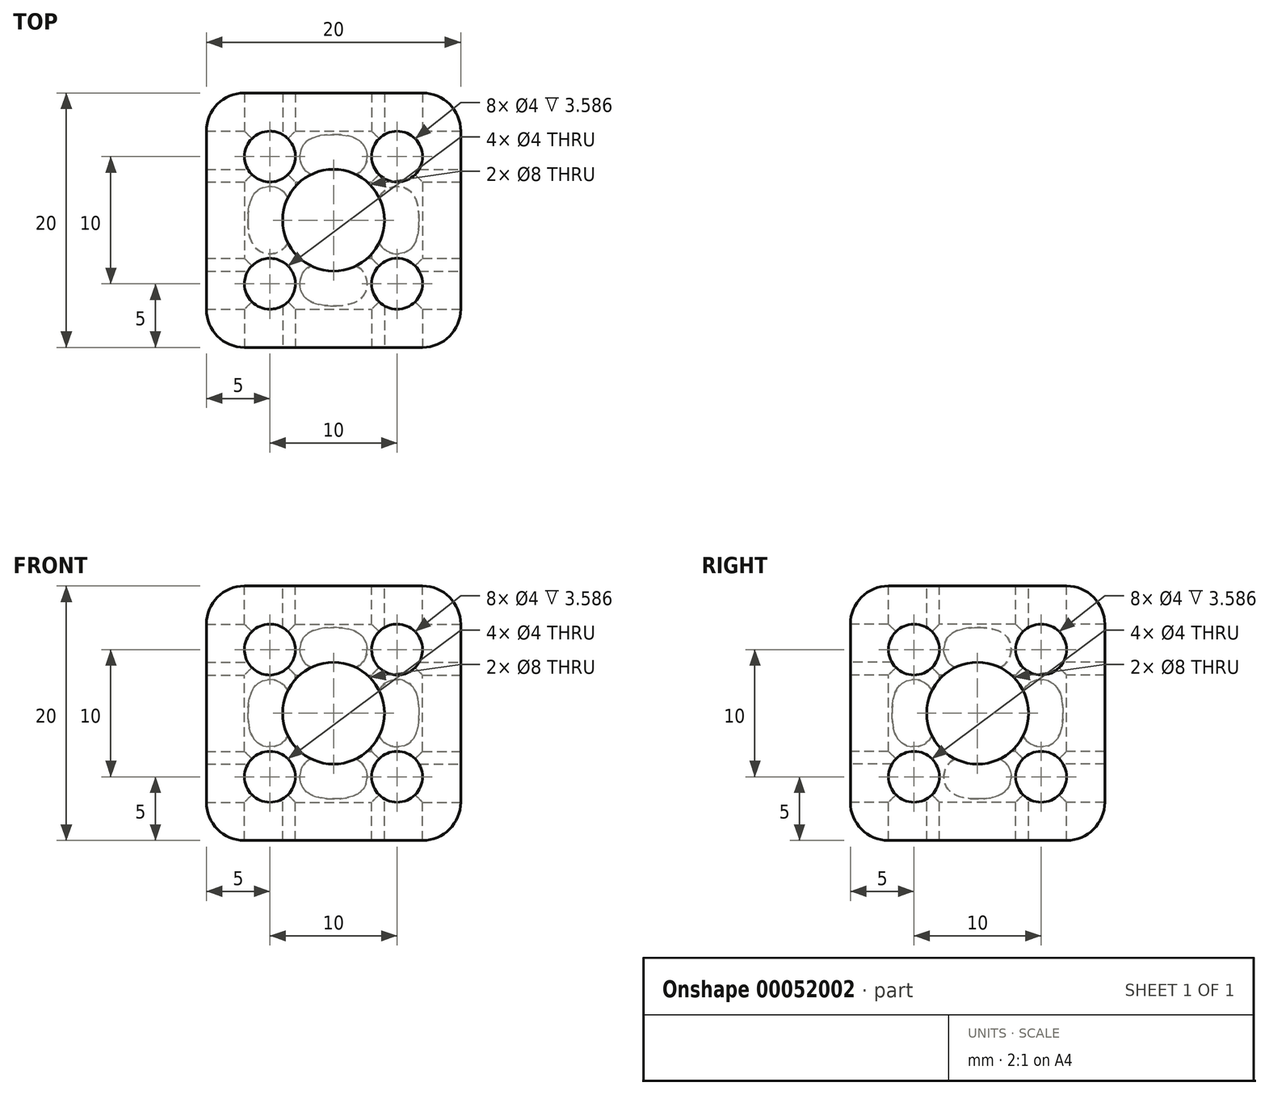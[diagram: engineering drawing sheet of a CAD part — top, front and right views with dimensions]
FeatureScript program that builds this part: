
annotation { "Feature Type Name" : "Feature", "Feature Type Description" : "" }
export const myFeature = defineFeature(function(context is Context, id is Id, definition is map)
    precondition{}
    {
        {
            var Q0;
            Q0=qCreatedBy(makeId("Top.planeOp"),FACE);
            var sketch = newSketch(context, id + "F0", { "sketchPlane" : qUnion([Q0])});
            skLineSegment(sketch, "E0.bottom", {"start": v(-10, 10) * mm, "end": v(10, 10) * mm});
            skLineSegment(sketch, "E0.top", {"start": v(-10, -10) * mm, "end": v(10, -10) * mm});
            skLineSegment(sketch, "E0.left", {"start": v(-10, 10) * mm, "end": v(-10, -10) * mm});
            skLineSegment(sketch, "E0.right", {"start": v(10, 10) * mm, "end": v(10, -10) * mm});
            skSolve(sketch);
        }
        {
            var Q0;
            Q0=makeQuery(id+"F0.imprint","IMPRINT",FACE,{"disambiguationData":[TD([[makeQuery(id+"F0.imprint","IMPRINT",EDGE,{"derivedFrom":sQuery(id+"F0.wireOp",EDGE,"E0.bottom")}),-1.0]])]});
            extrude(context, id + "F1", {"entities" : qUnion([Q0]), "endBound" : BoundingType.SYMMETRIC, "depth" : 20 * mm});
        }
        {
            var Q0;
            Q0=makeQuery(id+"F1.opExtrude","CAP_FACE",FACE,{"disambiguationData":[OSD([sQuery(id+"F0.wireOp",EDGE,"E0.bottom"),sQuery(id+"F0.wireOp",EDGE,"E0.top"),sQuery(id+"F0.wireOp",EDGE,"E0.left"),sQuery(id+"F0.wireOp",EDGE,"E0.right")])],"isStart":false});
            var sketch = newSketch(context, id + "F2", { "sketchPlane" : qUnion([Q0])});
            skLineSegment(sketch, "E1", {"start": v(-10, 10) * mm, "end": v(0, 0) * mm});
            skLineSegment(sketch, "E2", {"start": v(10, 10) * mm, "end": v(0, 0) * mm});
            skLineSegment(sketch, "E3", {"start": v(10, -10) * mm, "end": v(0, 0) * mm});
            skLineSegment(sketch, "E4", {"start": v(-10, -10) * mm, "end": v(0, 0) * mm});
            skPoint(sketch, "E5", {"position": v(-5, -5) * mm});
            skPoint(sketch, "E6", {"position": v(5, -5) * mm});
            skPoint(sketch, "E7", {"position": v(5, 5) * mm});
            skPoint(sketch, "E8", {"position": v(-5, 5) * mm});
            skSolve(sketch);
        }
        {
            var Q0;
            Q0=sQuery(id+"F2.wireOp",VERTEX,"E8");
            var Q1;
            Q1=sQuery(id+"F2.wireOp",VERTEX,"E7");
            var Q2;
            Q2=sQuery(id+"F2.wireOp",VERTEX,"E6");
            var Q3;
            Q3=sQuery(id+"F2.wireOp",VERTEX,"E5");
            var Q4;
            Q4=makeQuery(id+"F1.opExtrude","SWEPT_BODY",BODY,{"disambiguationData":[OSD([sQuery(id+"F0.wireOp",EDGE,"E0.bottom"),sQuery(id+"F0.wireOp",EDGE,"E0.top"),sQuery(id+"F0.wireOp",EDGE,"E0.left"),sQuery(id+"F0.wireOp",EDGE,"E0.right")])]});
            hole(context, id + "F3", {"style" : HoleStyle.SIMPLE, "holeDiameter" : 4 * mm, "endStyle" : HoleEndStyle.THROUGH, "locations" : qUnion([Q0, Q1, Q2, Q3]), "scope" : qUnion([Q4])});
        }
        {
            var Q0;
            Q0=makeQuery(id+"F1.opExtrude","SWEPT_FACE",FACE,{"disambiguationData":[OSD([sQuery(id+"F0.wireOp",EDGE,"E0.top")])]});
            var sketch = newSketch(context, id + "F4", { "sketchPlane" : qUnion([Q0])});
            skLineSegment(sketch, "E9", {"start": v(-10, 10) * mm, "end": v(0, 0) * mm});
            skLineSegment(sketch, "E10", {"start": v(10, 10) * mm, "end": v(0, 0) * mm});
            skLineSegment(sketch, "E11", {"start": v(10, -10) * mm, "end": v(0, 0) * mm});
            skLineSegment(sketch, "E12", {"start": v(-10, -10) * mm, "end": v(0, 0) * mm});
            skPoint(sketch, "E13", {"position": v(-5, -5) * mm});
            skPoint(sketch, "E14", {"position": v(-5, 5) * mm});
            skPoint(sketch, "E15", {"position": v(5, 5) * mm});
            skPoint(sketch, "E16", {"position": v(5, -5) * mm});
            skSolve(sketch);
        }
        {
            var Q0;
            Q0=sQuery(id+"F4.wireOp",VERTEX,"E14");
            var Q1;
            Q1=sQuery(id+"F4.wireOp",VERTEX,"E15");
            var Q2;
            Q2=sQuery(id+"F4.wireOp",VERTEX,"E16");
            var Q3;
            Q3=sQuery(id+"F4.wireOp",VERTEX,"E13");
            var Q4;
            Q4=makeQuery(id+"F1.opExtrude","SWEPT_BODY",BODY,{"disambiguationData":[OSD([sQuery(id+"F0.wireOp",EDGE,"E0.bottom"),sQuery(id+"F0.wireOp",EDGE,"E0.top"),sQuery(id+"F0.wireOp",EDGE,"E0.left"),sQuery(id+"F0.wireOp",EDGE,"E0.right")])]});
            hole(context, id + "F5", {"style" : HoleStyle.SIMPLE, "holeDiameter" : 4 * mm, "endStyle" : HoleEndStyle.THROUGH, "locations" : qUnion([Q0, Q1, Q2, Q3]), "scope" : qUnion([Q4])});
        }
        {
            var Q0;
            Q0=makeQuery(id+"F1.opExtrude","SWEPT_FACE",FACE,{"disambiguationData":[OSD([sQuery(id+"F0.wireOp",EDGE,"E0.right")])]});
            var sketch = newSketch(context, id + "F6", { "sketchPlane" : qUnion([Q0])});
            skLineSegment(sketch, "E17", {"start": v(-10, 10) * mm, "end": v(0, 0) * mm});
            skLineSegment(sketch, "E18", {"start": v(0, 0) * mm, "end": v(10, 10) * mm});
            skLineSegment(sketch, "E19", {"start": v(-10, -10) * mm, "end": v(0, 0) * mm});
            skLineSegment(sketch, "E20", {"start": v(10, -10) * mm, "end": v(0, 0) * mm});
            skPoint(sketch, "E21", {"position": v(-5, 5) * mm});
            skPoint(sketch, "E22", {"position": v(5, 5) * mm});
            skPoint(sketch, "E23", {"position": v(5, -5) * mm});
            skPoint(sketch, "E24", {"position": v(-5, -5) * mm});
            skSolve(sketch);
        }
        {
            var Q0;
            Q0=sQuery(id+"F6.wireOp",VERTEX,"E21");
            var Q1;
            Q1=sQuery(id+"F6.wireOp",VERTEX,"E22");
            var Q2;
            Q2=sQuery(id+"F6.wireOp",VERTEX,"E23");
            var Q3;
            Q3=sQuery(id+"F6.wireOp",VERTEX,"E24");
            var Q4;
            Q4=makeQuery(id+"F1.opExtrude","SWEPT_BODY",BODY,{"disambiguationData":[OSD([sQuery(id+"F0.wireOp",EDGE,"E0.bottom"),sQuery(id+"F0.wireOp",EDGE,"E0.top"),sQuery(id+"F0.wireOp",EDGE,"E0.left"),sQuery(id+"F0.wireOp",EDGE,"E0.right")])]});
            hole(context, id + "F7", {"style" : HoleStyle.SIMPLE, "holeDiameter" : 4 * mm, "endStyle" : HoleEndStyle.THROUGH, "locations" : qUnion([Q0, Q1, Q2, Q3]), "scope" : qUnion([Q4])});
        }
        {
            var Q0;
            Q0=makeQuery(id+"F1.opExtrude","CAP_EDGE",EDGE,{"disambiguationData":[OSD([sQuery(id+"F0.wireOp",EDGE,"E0.right")])],"isStart":false});
            var Q1;
            Q1=makeQuery(id+"F1.opExtrude","SWEPT_EDGE",EDGE,{"disambiguationData":[OSD([sQuery(id+"F0.wireOp",EDGE,"E0.top"),sQuery(id+"F0.wireOp",EDGE,"E0.right")])]});
            var Q2;
            Q2=makeQuery(id+"F1.opExtrude","SWEPT_EDGE",EDGE,{"disambiguationData":[OSD([sQuery(id+"F0.wireOp",EDGE,"E0.bottom"),sQuery(id+"F0.wireOp",EDGE,"E0.right")])]});
            var Q3;
            Q3=makeQuery(id+"F1.opExtrude","CAP_EDGE",EDGE,{"disambiguationData":[OSD([sQuery(id+"F0.wireOp",EDGE,"E0.right")])],"isStart":true});
            var Q4;
            Q4=makeQuery(id+"F1.opExtrude","CAP_EDGE",EDGE,{"disambiguationData":[OSD([sQuery(id+"F0.wireOp",EDGE,"E0.bottom")])],"isStart":false});
            var Q5;
            Q5=makeQuery(id+"F1.opExtrude","CAP_EDGE",EDGE,{"disambiguationData":[OSD([sQuery(id+"F0.wireOp",EDGE,"E0.top")])],"isStart":false});
            var Q6;
            Q6=makeQuery(id+"F1.opExtrude","CAP_EDGE",EDGE,{"disambiguationData":[OSD([sQuery(id+"F0.wireOp",EDGE,"E0.left")])],"isStart":false});
            var Q7;
            Q7=makeQuery(id+"F1.opExtrude","CAP_EDGE",EDGE,{"disambiguationData":[OSD([sQuery(id+"F0.wireOp",EDGE,"E0.bottom")])],"isStart":true});
            var Q8;
            Q8=makeQuery(id+"F1.opExtrude","SWEPT_EDGE",EDGE,{"disambiguationData":[OSD([sQuery(id+"F0.wireOp",EDGE,"E0.bottom"),sQuery(id+"F0.wireOp",EDGE,"E0.left")])]});
            var Q9;
            Q9=makeQuery(id+"F1.opExtrude","CAP_EDGE",EDGE,{"disambiguationData":[OSD([sQuery(id+"F0.wireOp",EDGE,"E0.left")])],"isStart":true});
            var Q10;
            Q10=makeQuery(id+"F1.opExtrude","CAP_EDGE",EDGE,{"disambiguationData":[OSD([sQuery(id+"F0.wireOp",EDGE,"E0.top")])],"isStart":true});
            var Q11;
            Q11=makeQuery(id+"F1.opExtrude","SWEPT_EDGE",EDGE,{"disambiguationData":[OSD([sQuery(id+"F0.wireOp",EDGE,"E0.top"),sQuery(id+"F0.wireOp",EDGE,"E0.left")])]});
            fillet(context, id + "F8", {"entities" : qUnion([Q0, Q1, Q2, Q3, Q4, Q5, Q6, Q7, Q8, Q9, Q10, Q11]), "radius" : 3 * mm, "tangentPropagation" : true, "allowEdgeOverflow" : false});
        }
        {
            var Q0;
            Q0=makeQuery(id+"F1.opExtrude","CAP_FACE",FACE,{"disambiguationData":[OSD([sQuery(id+"F0.wireOp",EDGE,"E0.bottom"),sQuery(id+"F0.wireOp",EDGE,"E0.top"),sQuery(id+"F0.wireOp",EDGE,"E0.left"),sQuery(id+"F0.wireOp",EDGE,"E0.right")])],"isStart":false});
            var sketch = newSketch(context, id + "F9", { "sketchPlane" : qUnion([Q0])});
            skPoint(sketch, "E25", {"position": v(0, 0) * mm});
            skSolve(sketch);
        }
        {
            var Q0;
            Q0=sQuery(id+"F9.wireOp",VERTEX,"E25");
            var Q1;
            Q1=makeQuery(id+"F1.opExtrude","SWEPT_BODY",BODY,{"disambiguationData":[OSD([sQuery(id+"F0.wireOp",EDGE,"E0.bottom"),sQuery(id+"F0.wireOp",EDGE,"E0.top"),sQuery(id+"F0.wireOp",EDGE,"E0.left"),sQuery(id+"F0.wireOp",EDGE,"E0.right")])]});
            hole(context, id + "F10", {"style" : HoleStyle.SIMPLE, "holeDiameter" : 8 * mm, "endStyle" : HoleEndStyle.THROUGH, "locations" : qUnion([Q0]), "scope" : qUnion([Q1])});
        }
        {
            var Q0;
            Q0=makeQuery(id+"F1.opExtrude","SWEPT_FACE",FACE,{"disambiguationData":[OSD([sQuery(id+"F0.wireOp",EDGE,"E0.top")])]});
            var sketch = newSketch(context, id + "F11", { "sketchPlane" : qUnion([Q0])});
            skPoint(sketch, "E26", {"position": v(0, 0) * mm});
            skSolve(sketch);
        }
        {
            var Q0;
            Q0=sQuery(id+"F11.wireOp",VERTEX,"E26");
            var Q1;
            Q1=makeQuery(id+"F1.opExtrude","SWEPT_BODY",BODY,{"disambiguationData":[OSD([sQuery(id+"F0.wireOp",EDGE,"E0.bottom"),sQuery(id+"F0.wireOp",EDGE,"E0.top"),sQuery(id+"F0.wireOp",EDGE,"E0.left"),sQuery(id+"F0.wireOp",EDGE,"E0.right")])]});
            hole(context, id + "F12", {"style" : HoleStyle.SIMPLE, "holeDiameter" : 8 * mm, "endStyle" : HoleEndStyle.THROUGH, "locations" : qUnion([Q0]), "scope" : qUnion([Q1])});
        }
        {
            var Q0;
            Q0=makeQuery(id+"F1.opExtrude","SWEPT_FACE",FACE,{"disambiguationData":[OSD([sQuery(id+"F0.wireOp",EDGE,"E0.right")])]});
            var sketch = newSketch(context, id + "F13", { "sketchPlane" : qUnion([Q0])});
            skPoint(sketch, "E27", {"position": v(0, 0) * mm});
            skSolve(sketch);
        }
        {
            var Q0;
            Q0=sQuery(id+"F13.wireOp",VERTEX,"E27");
            var Q1;
            Q1=makeQuery(id+"F1.opExtrude","SWEPT_BODY",BODY,{"disambiguationData":[OSD([sQuery(id+"F0.wireOp",EDGE,"E0.bottom"),sQuery(id+"F0.wireOp",EDGE,"E0.top"),sQuery(id+"F0.wireOp",EDGE,"E0.left"),sQuery(id+"F0.wireOp",EDGE,"E0.right")])]});
            hole(context, id + "F14", {"style" : HoleStyle.SIMPLE, "holeDiameter" : 8 * mm, "endStyle" : HoleEndStyle.THROUGH, "locations" : qUnion([Q0]), "scope" : qUnion([Q1])});
        }
    });
